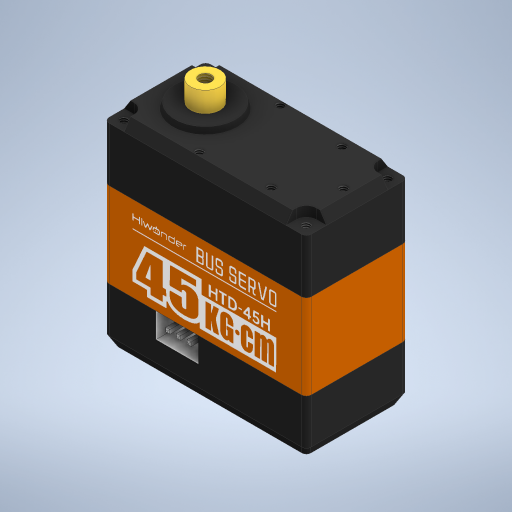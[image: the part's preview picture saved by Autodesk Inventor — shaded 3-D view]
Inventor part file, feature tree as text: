
AUTODESK INVENTOR PART (.ipt)
format: ipt  version: 2024.1 (Build 281209000, 209)  size: 1,343,488 bytes
history: native  units: in
note: dims shown in document units (in); Inventor stores cm internally (conversion verified against a paired STEP export)
features: sketch x24, extrude x9, split x8, chamfer x7, other x5, hole x5, projected_geometry x5, plane x3, move_body x2, fillet x1
ambient origin geometry x8: Origin, YZ Plane, XZ Plane, XY Plane, X Axis, Y Axis, Z Axis, Center Point
bodies: Solid1 (feature_tree)
feature tree (69):
  other  "HTD-45H"
  extrude  "Extrusion1"  Depth=0.7929in
  extrude  "Extrusion2"  Depth=0.3937in
  extrude  "Extrusion3"  Depth=0.0433in TaperAngle=0.0deg
  hole  "Hole1"  [1 undecoded]
  extrude  "Extrusion5"  Depth=0.0787in
  chamfer  "Chamfer1"  Distance=0.0787in
  chamfer  "Chamfer2"  Distance=0.0787in Angle=45.0deg
  chamfer  "Chamfer3"  Distance=0.0394in Angle=45.0deg
  extrude  "Extrusion6"  Depth=0.0433in
  extrude  "Extrusion7"  Depth=0.2362in
  chamfer  "Chamfer4"  Distance=0.1449in
  extrude  "Extrusion8"  Depth=0.4299in
  chamfer  "Chamfer5"  Distance=0.2362in
  extrude  "Extrusion9"  Depth=0.0315in
  chamfer  "Chamfer6"  Distance=0.0098in Angle=45.0deg
  extrude  "Extrusion10"  Depth=0.2362in TaperAngle=45.0deg
  chamfer  "Chamfer7"  Distance=0.0315in
  hole  "Hole2"  [1 undecoded]
  hole  "Hole3"  [1 undecoded]
  hole  "Hole4"  [1 undecoded]
  hole  "Hole5"  [1 undecoded]
  split  "Split1"
  split  "Split2"
  split  "Split3"
  split  "Split4"
  split  "Split5"
  split  "Split6"
  split  "Split7"
  split  "Split8"
  fillet  "Fillet3"  Radius=0.0098in
  move_body  "Move Body1"
  move_body  "Move Body2"
  other  "Decal1"
  other  "Decal2"
  plane  "Work Plane2"
  plane  "Work Plane3"
  plane  "Work Plane4"
  sketch  "Sketch1"  dims[d0=1.5787in d1=0.7929in]
  sketch  "Sketch2"  dims[d2=1.5945in d3=0.0in d4=0.3937in]
  sketch  "Sketch3"  dims[d5=0.5039in d6=0.0433in d7=0.0in]
  sketch  "Sketch5"  dims[d8=0.2303in d9=0.1602in d10=0.0in]
  projected_geometry  "Projected Loop2"
  sketch  "Sketch6"  dims[d14=0.0787in d15=0.0787in]
  projected_geometry  "Projected Loop3"
  projected_geometry  "Projected Loop4"
  projected_geometry  "Projected Loop5"
  sketch  "Sketch7"  dims[d16=0.0787in]
  sketch  "Sketch8"  dims[d17=0.0787in]
  sketch  "Sketch9"  dims[d18=0.0617in d19=1.2598in d20=0.1732in d21=0.0787in d22=90.0deg d23=1.2598in d24=0.0in]
  sketch  "Sketch10"  dims[d25=0.1575in d26=0.0787in d27=0.0in d28=0.0504in d29=0.0787in d30=45.0deg d31=0.0394in d32=0.0787in d33=45.0deg]
  projected_geometry  "Projected Loop6"
  sketch  "Sketch11"  dims[d35=0.0433in d36=0.0157in d37=45.0deg d38=0.5039in]
  sketch  "Sketch12"  dims[d39=0.0634in d40=0.0in d41=0.2362in d42=0.1449in d43=0.0in]
  sketch  "Sketch13"  dims[d44=0.0634in d45=0.0157in d46=45.0deg d48=0.4299in]
  sketch  "Sketch14"  dims[d51=0.2362in]
  sketch  "Sketch15"  dims[d52=0.3327in d53=0.2362in d54=0.0in]
  sketch  "Sketch16"  dims[d55=0.0315in d56=0.0315in]
  sketch  "Sketch18"  dims[d57=0.0315in]
  sketch  "Sketch19"  dims[d58=0.0315in]
  sketch  "Sketch20"  dims[d59=0.0315in]
  sketch  "Sketch21"  dims[d60=0.0315in d61=0.0098in d62=0.0157in d63=45.0deg]
  sketch  "Sketch22"  dims[d64=0.2362in d65=0.0in d66=0.0098in d67=0.0157in d68=45.0deg]
  sketch  "Sketch23"  dims[d69=0.3327in]
  sketch  "Sketch24"  dims[d70=0.2362in]
  sketch  "Sketch25"  dims[d71=0.0315in]
  other  "Image1"
  sketch  "Sketch26"  dims[d72=0.0315in d73=0.0315in d74=0.0315in d75=0.0315in d76=0.0315in d77=0.2362in d78=0.0in d79=0.0098in d80=0.0157in d81=45.0deg d83=0.5008in d84=0.0968in d85=0.1602in d86=0.1575in d87=0.0787in d88=90.0deg d89=0.0315in d90=0.0in d91=0.0968in d92=0.1449in d93=0.1575in d94=0.0787in d95=90.0deg d96=0.315in d97=0.0in d98=0.2717in d99=0.5205in d100=0.2874in d101=0.6299in d102=0.5512in d103=0.0617in d104=0.1969in d105=0.1575in d106=0.0787in d107=90.0deg d108=0.1969in d109=0.0in d110=0.0984in d111=0.5925in d112=0.7874in d113=0.5945in d114=0.0617in d115=0.1969in d116=0.1575in d117=0.0787in d118=90.0deg d119=0.1969in d120=0.0in d122=0.4055in d123=0.8406in d124=0.0394in d160=1.3386in d184=1.3386in d190=0.0in d191=-1.798in d192=0.0in d193=0.3957in d194=0.0in d195=0.0in d125=0.0in d126=0.0in d127=0.0in]
  other  "Image2"
note: 5 required parameter values undecoded (feature->parameter linkage not recoverable at this tier; creation-order binding heuristic only, values carry confidence <= 0.55)
